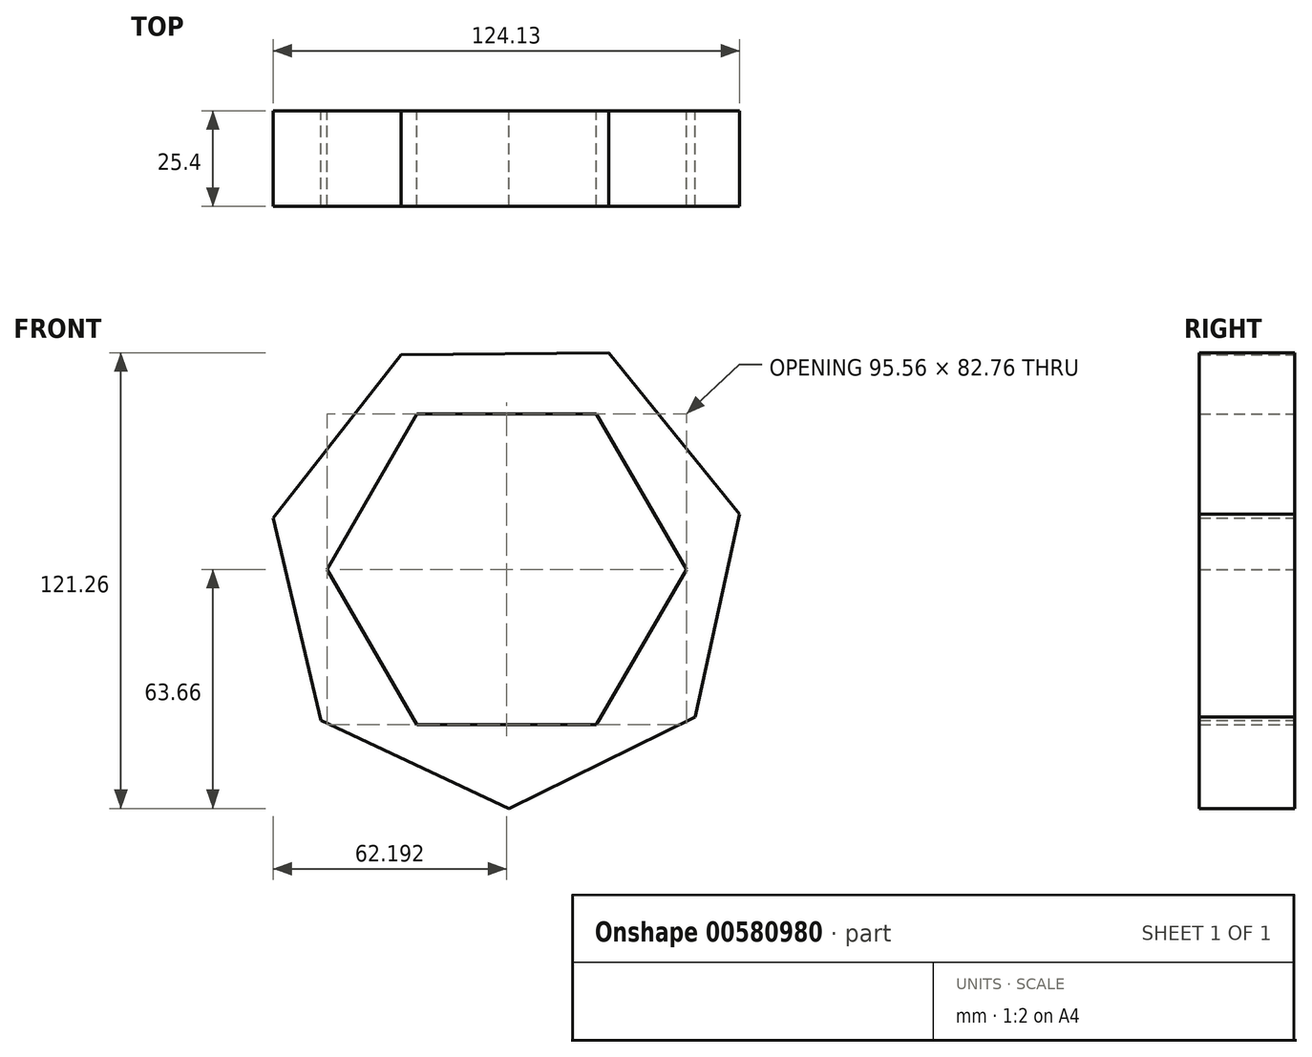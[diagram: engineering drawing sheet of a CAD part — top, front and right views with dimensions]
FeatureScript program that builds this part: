
annotation { "Feature Type Name" : "Feature", "Feature Type Description" : "" }
export const myFeature = defineFeature(function(context is Context, id is Id, definition is map)
    precondition{}
    {
        {
            var Q0;
            Q0=qCreatedBy(makeId("Front.planeOp"),FACE);
            var sketch = newSketch(context, id + "F0", { "sketchPlane" : qUnion([Q0])});
            skCircle(sketch, "E0.cCircle", {"center": v(3.51, 0) * mm, "radius": 41.38 * mm, "construction": true});
            skLineSegment(sketch, "E0.0", {"start": v(27.4, -41.38) * mm, "end": v(-20.38, -41.38) * mm});
            skLineSegment(sketch, "E0.1", {"start": v(-20.38, -41.38) * mm, "end": v(-44.27, 0) * mm});
            skLineSegment(sketch, "E0.2", {"start": v(-44.27, 0) * mm, "end": v(-20.38, 41.38) * mm});
            skLineSegment(sketch, "E0.3", {"start": v(-20.38, 41.38) * mm, "end": v(27.4, 41.38) * mm});
            skLineSegment(sketch, "E0.4", {"start": v(27.4, 41.38) * mm, "end": v(51.3, 0) * mm});
            skLineSegment(sketch, "E0.5", {"start": v(51.3, 0) * mm, "end": v(27.4, -41.38) * mm});
            skPoint(sketch, "E0.0.midPoint", {"position": v(3.51, -41.38) * mm});
            skCircle(sketch, "E1.cCircle", {"center": v(3.51, 0) * mm, "radius": 57.36 * mm, "construction": true});
            skLineSegment(sketch, "E1.0", {"start": v(53.64, -39.25) * mm, "end": v(4.08, -63.66) * mm});
            skLineSegment(sketch, "E1.1", {"start": v(4.08, -63.66) * mm, "end": v(-45.9, -40.14) * mm});
            skLineSegment(sketch, "E1.2", {"start": v(-45.9, -40.14) * mm, "end": v(-58.68, 13.61) * mm});
            skLineSegment(sketch, "E1.3", {"start": v(-58.68, 13.61) * mm, "end": v(-24.62, 57.11) * mm});
            skLineSegment(sketch, "E1.4", {"start": v(-24.62, 57.11) * mm, "end": v(30.62, 57.6) * mm});
            skLineSegment(sketch, "E1.5", {"start": v(30.62, 57.6) * mm, "end": v(65.45, 14.72) * mm});
            skLineSegment(sketch, "E1.6", {"start": v(65.45, 14.72) * mm, "end": v(53.64, -39.25) * mm});
            skPoint(sketch, "E1.0.midPoint", {"position": v(28.86, -51.46) * mm});
            skSolve(sketch);
        }
        {
            var Q0;
            Q0=makeQuery(id+"F0.imprint","IMPRINT",FACE,{"disambiguationData":[TD([[makeQuery(id+"F0.imprint","IMPRINT",EDGE,{"derivedFrom":sQuery(id+"F0.wireOp",EDGE,"E0.0")}),1.0]])]});
            extrude(context, id + "F1", {"entities" : qUnion([Q0]), "depth" : 25.4 * mm, "offsetDistance" : 25.4 * mm});
        }
    });
